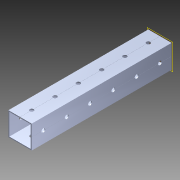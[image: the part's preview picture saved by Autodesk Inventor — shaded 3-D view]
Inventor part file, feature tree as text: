
AUTODESK INVENTOR PART (.ipt)
format: ipt  version: 2014 (Build 180170000, 170)  size: 1,147,904 bytes
history: native  units: in
note: dims shown in document units (in); Inventor stores cm internally (conversion verified against a paired STEP export)
features: pattern_circular x1, other x1, plane x1, extrude x1, imported_body x1, sketch x1
ambient origin geometry x8: Origin, YZ Plane, XZ Plane, XY Plane, X Axis, Y Axis, Z Axis, Center Point
bodies: Body1 (feature_tree)
feature tree (6):
  pattern_circular  "CirPattern2"
  other  "217-3426-STEP1"
  plane  "Work Plane1"
  extrude  "Extrusion1"  Depth=3937.0079in TaperAngle=0.0deg
  imported_body  "Base1"
  sketch  "Sketch1"  dims[d0=-6.0in d1=3937.0079in d2=0.0in]
